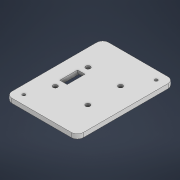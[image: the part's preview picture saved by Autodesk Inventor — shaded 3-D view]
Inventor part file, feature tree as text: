
AUTODESK INVENTOR PART (.ipt)
format: ipt  version: 2022 (Build 260153000, 153)  size: 133,632 bytes
history: native  units: in
note: dims shown in document units (in); Inventor stores cm internally (conversion verified against a paired STEP export)
features: extrude x2, sketch x2
ambient origin geometry x8: Origin, YZ Plane, XZ Plane, XY Plane, X Axis, Y Axis, Z Axis, Center Point
bodies: Solid1 (feature_tree)
feature tree (4):
  extrude  "Extrusion1"  Depth=2.5591in
  extrude  "Extrusion2"  Depth=0.1181in TaperAngle=0.0deg
  sketch  "Sketch1"  dims[d0=1.8898in d1=2.5591in]
  sketch  "Sketch3"  dims[d3=0.1575in d17=0.1181in d18=0.0in d20=0.1969in d21=0.4724in d22=0.0787in d23=0.0in d19=0.0197in d27=0.0197in d28=0.0344in d29=0.0197in d30=0.0344in]
